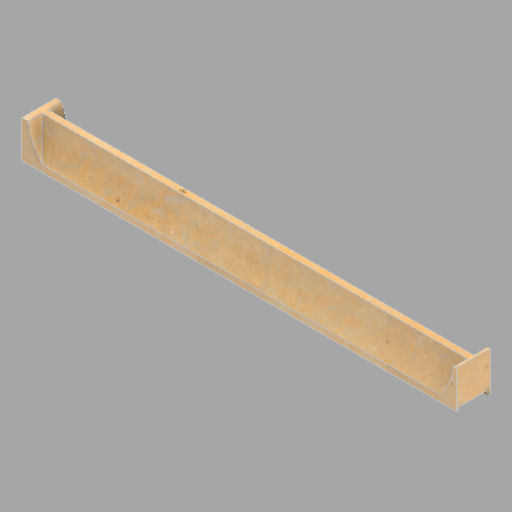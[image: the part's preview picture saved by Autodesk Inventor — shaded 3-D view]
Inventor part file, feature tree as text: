
AUTODESK INVENTOR PART (.ipt)
format: ipt  version: 2022.2 (Build 262287010, 287A)  size: 200,704 bytes
history: native  units: in
note: dims shown in document units (in); Inventor stores cm internally (conversion verified against a paired STEP export)
features: direct_edit x1, revolve x1
ambient origin geometry x8: Origin, YZ Plane, XZ Plane, XY Plane, X Axis, Y Axis, Z Axis, Center Point
bodies: Solid1 (feature_tree), Body1 (feature_tree)
feature tree (2):
  direct_edit  "Direct Edit1"
  revolve  "Rotate1"  Angle=180.0deg
